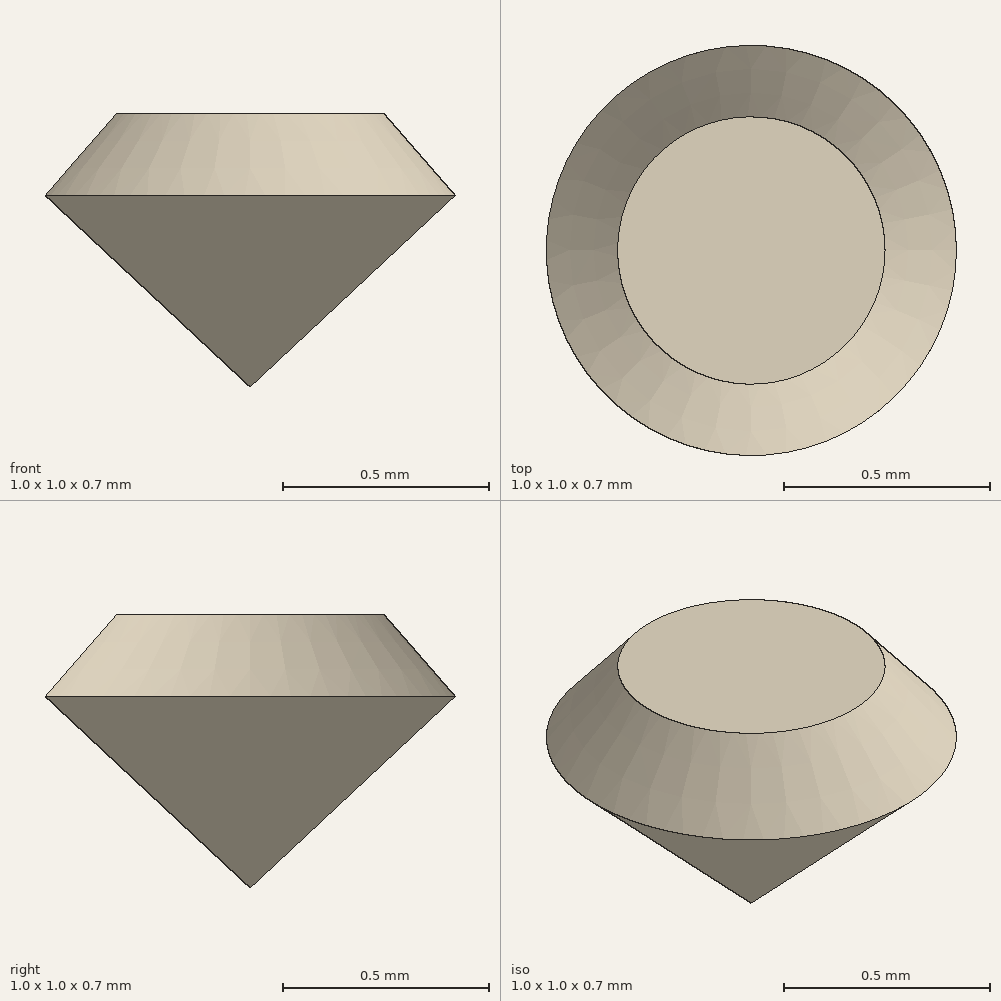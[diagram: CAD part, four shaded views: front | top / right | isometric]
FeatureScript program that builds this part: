
annotation { "Feature Type Name" : "Feature", "Feature Type Description" : "" }
export const myFeature = defineFeature(function(context is Context, id is Id, definition is map)
    precondition{}
    {
        {
            var Q0;
            Q0=qCreatedBy(makeId("Front.planeOp"),FACE);
            var sketch = newSketch(context, id + "F0", { "sketchPlane" : qUnion([Q0])});
            skLineSegment(sketch, "E0", {"start": v(0, 0.64) * mm, "end": v(0, -0.79) * mm, "construction": true});
            skLineSegment(sketch, "E1", {"start": v(0, 0.2) * mm, "end": v(0.33, 0.2) * mm});
            skLineSegment(sketch, "E2", {"start": v(0.33, 0.2) * mm, "end": v(0.5, 0) * mm});
            skLineSegment(sketch, "E3", {"start": v(0.5, 0) * mm, "end": v(0, -0.47) * mm});
            skLineSegment(sketch, "E4", {"start": v(0, -0.47) * mm, "end": v(0, 0.2) * mm});
            skSolve(sketch);
        }
        {
            var Q0;
            Q0 = qSketchRegion(id + "F0", true);
            var Q1;
            Q1=sQuery(id+"F0.wireOp",EDGE,"E0");
            revolve(context, id + "F1", {"entities" : qUnion([Q0]), "axis" : qUnion([Q1]), "revolveType" : RevolveType.FULL});
        }
    });
